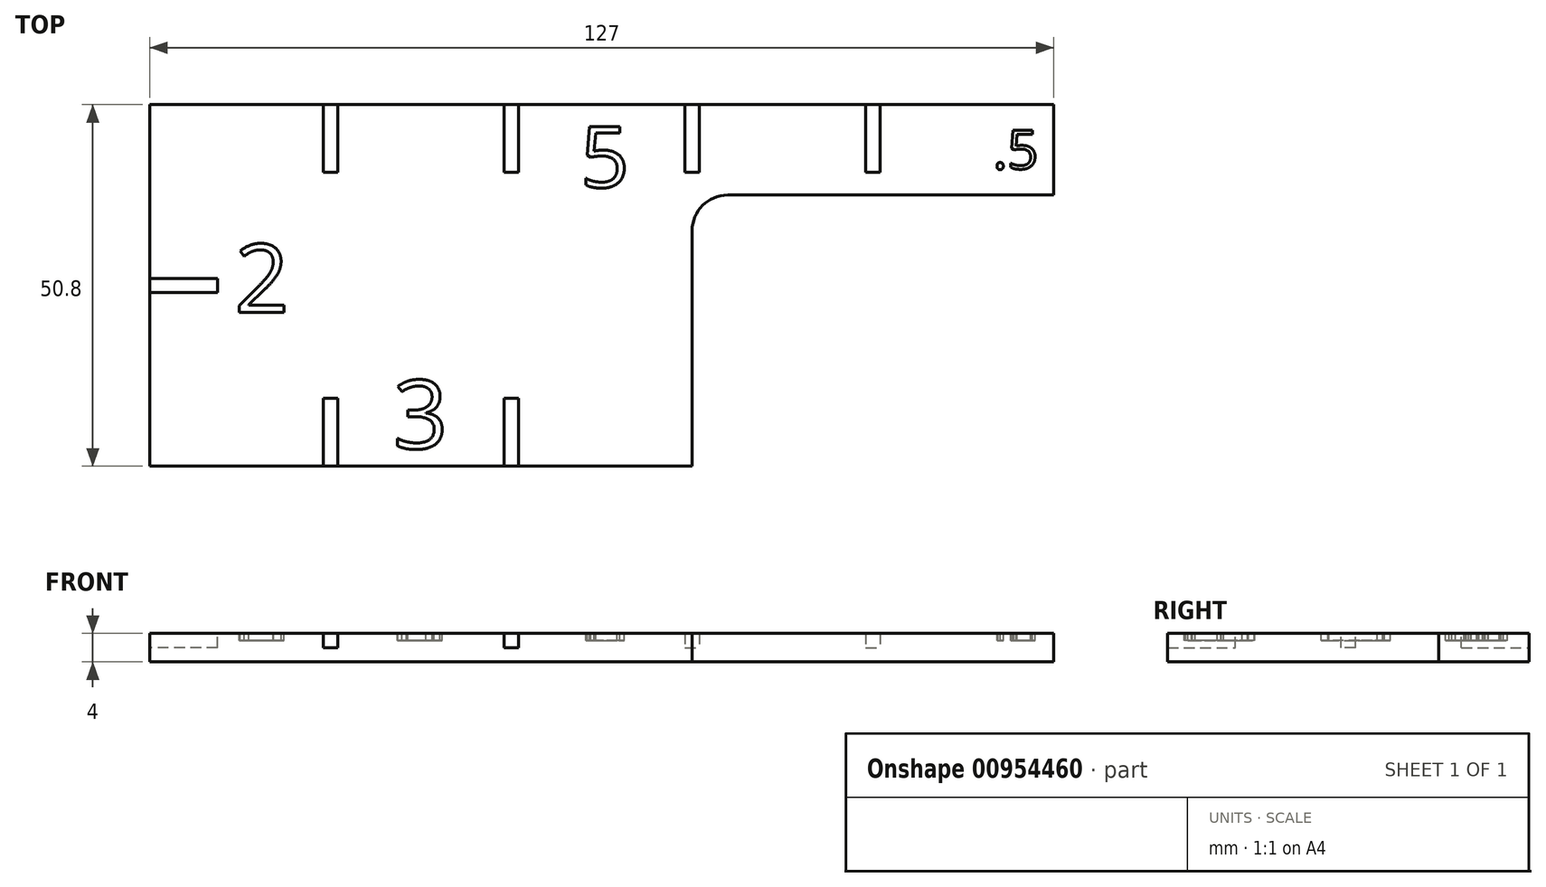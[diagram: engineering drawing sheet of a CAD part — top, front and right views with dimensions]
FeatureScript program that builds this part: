
annotation { "Feature Type Name" : "Feature", "Feature Type Description" : "" }
export const myFeature = defineFeature(function(context is Context, id is Id, definition is map)
    precondition{}
    {
        {
            var Q0;
            Q0=qCreatedBy(makeId("Top.planeOp"),FACE);
            var sketch = newSketch(context, id + "F0", { "sketchPlane" : qUnion([Q0])});
            skLineSegment(sketch, "E0.top", {"start": v(-38.1, -25.4) * mm, "end": v(38.1, -25.4) * mm});
            skLineSegment(sketch, "E0.left", {"start": v(-38.1, 25.4) * mm, "end": v(-38.1, -25.4) * mm});
            skPoint(sketch, "E0.middle", {"position": v(0, 0) * mm});
            skLineSegment(sketch, "E1.right", {"start": v(88.9, 25.4) * mm, "end": v(88.9, 12.7) * mm});
            skLineSegment(sketch, "E2", {"start": v(-38.1, 25.4) * mm, "end": v(88.9, 25.4) * mm});
            skLineSegment(sketch, "E3", {"start": v(38.1, -25.4) * mm, "end": v(38.1, 7.7) * mm});
            skLineSegment(sketch, "E4", {"start": v(43.1, 12.7) * mm, "end": v(88.9, 12.7) * mm});
            skPoint(sketch, "E5.visualSharp", {"position": v(38.1, 12.7) * mm});
            skArc(sketch, "E5.filletArc", {"start": v(43.1, 12.7) * mm, "mid": v(39.56, 11.24) * mm, "end": v(38.1, 7.7) * mm});
            skSolve(sketch);
        }
        {
            var Q0;
            Q0=qSketchRegion(id+"F0",true);
            extrude(context, id + "F1", {"entities" : qUnion([Q0]), "depth" : 4 * mm, "offsetDistance" : 25 * mm});
        }
        {
            var Q0;
            Q0=makeQuery(id+"F1.opExtrude","CAP_FACE",FACE,{"disambiguationData":[OSD([sQuery(id+"F0.wireOp",EDGE,"E0.bottom"),sQuery(id+"F0.wireOp",EDGE,"E0.top"),sQuery(id+"F0.wireOp",EDGE,"E0.left"),sQuery(id+"F0.wireOp",EDGE,"E1.bottom"),sQuery(id+"F0.wireOp",EDGE,"E1.top"),sQuery(id+"F0.wireOp",EDGE,"E1.right"),sQuery(id+"F0.wireOp",EDGE,"bVqaHpRX-HDwA-xkqE-OFi6-3U84sKLk9Oys"),sQuery(id+"F0.wireOp",EDGE,"a1d024c4-d531-45f1-a03b-53352d4f72b3.filletArc")])],"isStart":false});
            var sketch = newSketch(context, id + "F2", { "sketchPlane" : qUnion([Q0])});
            skLineSegment(sketch, "E6.bottom", {"start": v(-11.7, 15.88) * mm, "end": v(-13.7, 15.88) * mm});
            skLineSegment(sketch, "E6.top", {"start": v(-11.7, 34.93) * mm, "end": v(-13.7, 34.93) * mm});
            skLineSegment(sketch, "E6.left", {"start": v(-11.7, 15.88) * mm, "end": v(-11.7, 34.93) * mm});
            skLineSegment(sketch, "E6.right", {"start": v(-13.7, 15.88) * mm, "end": v(-13.7, 34.93) * mm});
            skPoint(sketch, "E6.middle", {"position": v(-12.7, 25.4) * mm});
            skLineSegment(sketch, "E7.bottom", {"start": v(13.7, 15.88) * mm, "end": v(11.7, 15.88) * mm});
            skLineSegment(sketch, "E7.top", {"start": v(13.7, 34.93) * mm, "end": v(11.7, 34.93) * mm});
            skLineSegment(sketch, "E7.left", {"start": v(13.7, 15.88) * mm, "end": v(13.7, 34.93) * mm});
            skLineSegment(sketch, "E7.right", {"start": v(11.7, 15.88) * mm, "end": v(11.7, 34.93) * mm});
            skPoint(sketch, "E7.middle", {"position": v(12.7, 25.4) * mm});
            skLineSegment(sketch, "E8.bottom", {"start": v(39.1, 15.88) * mm, "end": v(37.1, 15.88) * mm});
            skLineSegment(sketch, "E8.top", {"start": v(39.1, 34.93) * mm, "end": v(37.1, 34.93) * mm});
            skLineSegment(sketch, "E8.left", {"start": v(39.1, 15.88) * mm, "end": v(39.1, 34.93) * mm});
            skLineSegment(sketch, "E8.right", {"start": v(37.1, 15.88) * mm, "end": v(37.1, 34.93) * mm});
            skPoint(sketch, "E8.middle", {"position": v(38.1, 25.4) * mm});
            skLineSegment(sketch, "E9.bottom", {"start": v(64.5, 15.88) * mm, "end": v(62.5, 15.88) * mm});
            skLineSegment(sketch, "E9.top", {"start": v(64.5, 34.93) * mm, "end": v(62.5, 34.93) * mm});
            skLineSegment(sketch, "E9.left", {"start": v(64.5, 15.88) * mm, "end": v(64.5, 34.93) * mm});
            skLineSegment(sketch, "E9.right", {"start": v(62.5, 15.88) * mm, "end": v(62.5, 34.93) * mm});
            skPoint(sketch, "E9.middle", {"position": v(63.5, 25.4) * mm});
            skLineSegment(sketch, "E10.bottom", {"start": v(-28.58, 1) * mm, "end": v(-28.58, -1) * mm});
            skLineSegment(sketch, "E10.top", {"start": v(-47.62, 1) * mm, "end": v(-47.62, -1) * mm});
            skLineSegment(sketch, "E10.left", {"start": v(-28.58, 1) * mm, "end": v(-47.62, 1) * mm});
            skLineSegment(sketch, "E10.right", {"start": v(-28.58, -1) * mm, "end": v(-47.62, -1) * mm});
            skPoint(sketch, "E10.middle", {"position": v(-38.1, 0) * mm});
            skLineSegment(sketch, "E11.bottom", {"start": v(-11.7, -34.93) * mm, "end": v(-13.7, -34.93) * mm});
            skLineSegment(sketch, "E11.top", {"start": v(-11.7, -15.88) * mm, "end": v(-13.7, -15.88) * mm});
            skLineSegment(sketch, "E11.left", {"start": v(-11.7, -34.92) * mm, "end": v(-11.7, -15.88) * mm});
            skLineSegment(sketch, "E11.right", {"start": v(-13.7, -34.93) * mm, "end": v(-13.7, -15.87) * mm});
            skPoint(sketch, "E11.middle", {"position": v(-12.7, -25.4) * mm});
            skLineSegment(sketch, "E12.bottom", {"start": v(13.7, -34.93) * mm, "end": v(11.7, -34.93) * mm});
            skLineSegment(sketch, "E12.top", {"start": v(13.7, -15.87) * mm, "end": v(11.7, -15.87) * mm});
            skLineSegment(sketch, "E12.left", {"start": v(13.7, -34.93) * mm, "end": v(13.7, -15.88) * mm});
            skLineSegment(sketch, "E12.right", {"start": v(11.7, -34.93) * mm, "end": v(11.7, -15.88) * mm});
            skPoint(sketch, "E12.middle", {"position": v(12.7, -25.4) * mm});
            skSolve(sketch);
        }
        {
            var Q0;
            Q0=qSketchRegion(id+"F2",true);
            extrude(context, id + "F3", {"entities" : qUnion([Q0]), "operationType" : NewBodyOperationType.REMOVE, "oppositeDirection" : true, "depth" : 2 * mm, "offsetDistance" : 25 * mm});
        }
        {
            var Q0;
            Q0=makeQuery(id+"F1.opExtrude","CAP_FACE",FACE,{"disambiguationData":[OSD([sQuery(id+"F0.wireOp",EDGE,"E0.bottom"),sQuery(id+"F0.wireOp",EDGE,"E0.top"),sQuery(id+"F0.wireOp",EDGE,"E0.left"),sQuery(id+"F0.wireOp",EDGE,"E1.bottom"),sQuery(id+"F0.wireOp",EDGE,"E1.top"),sQuery(id+"F0.wireOp",EDGE,"E1.right"),sQuery(id+"F0.wireOp",EDGE,"bVqaHpRX-HDwA-xkqE-OFi6-3U84sKLk9Oys"),sQuery(id+"F0.wireOp",EDGE,"a1d024c4-d531-45f1-a03b-53352d4f72b3.filletArc")])],"isStart":false});
            var sketch = newSketch(context, id + "F4", { "sketchPlane" : qUnion([Q0])});
            skText(sketch, "E13", { "text": "5", "fontName": "OpenSans-Regular.ttf"});
            skText(sketch, "E14", { "text": "3", "fontName": "OpenSans-Regular.ttf"});
            skText(sketch, "E15", { "text": "2", "fontName": "OpenSans-Regular.ttf"});
            skText(sketch, "E16", { "text": ".5", "fontName": "OpenSans-Regular.ttf"});
            const initialGuessF4  = {"E13": [0.02241, 0.01379, 1, 0, 0.00862], "E14": [-0.00391, -0.02292, 1, 0, 0.00967], "E15": [-0.0262, -0.0038, 1, 0, 0.00967], "E16": [0.08037, 0.01638, 1, 0, 0.00546]};
            skSetInitialGuess(sketch, initialGuessF4);
            skSolve(sketch);
        }
        {
            var Q0;
            Q0 = qSketchRegion(id + "F4", true);
            extrude(context, id + "F5", {"entities" : qUnion([Q0]), "operationType" : NewBodyOperationType.REMOVE, "oppositeDirection" : true, "depth" : 1 * mm, "offsetDistance" : 25 * mm});
        }
    });
